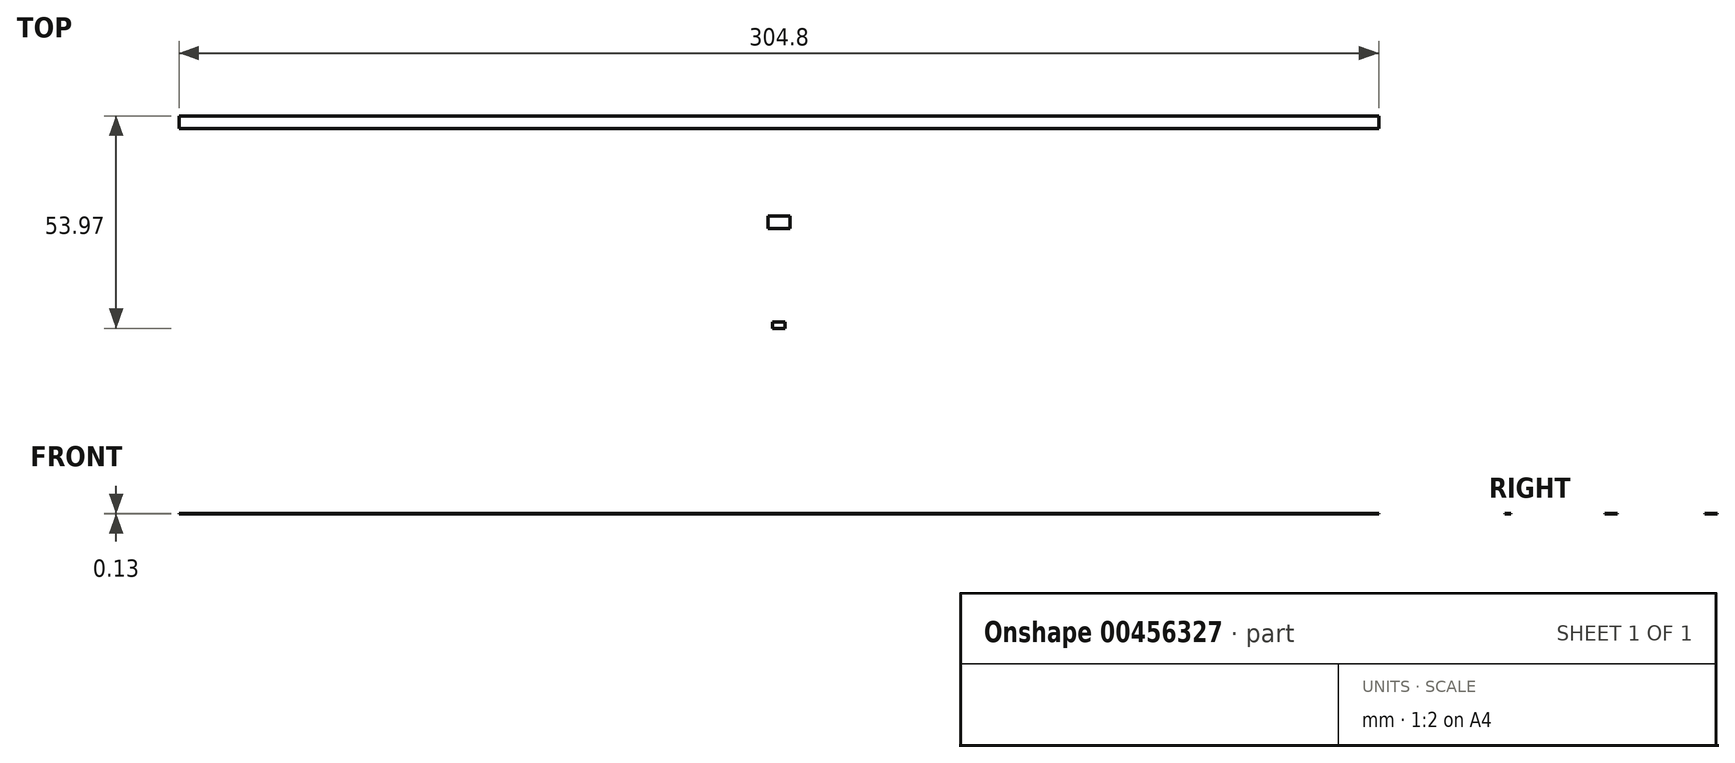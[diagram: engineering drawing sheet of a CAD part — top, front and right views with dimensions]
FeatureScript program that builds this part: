
annotation { "Feature Type Name" : "Feature", "Feature Type Description" : "" }
export const myFeature = defineFeature(function(context is Context, id is Id, definition is map)
    precondition{}
    {
        {
            var Q0;
            Q0=qCreatedBy(makeId("Top.planeOp"),FACE);
            var sketch = newSketch(context, id + "F0", { "sketchPlane" : qUnion([Q0])});
            skPoint(sketch, "E0", {"position": v(0, 0) * mm});
            skPoint(sketch, "E1", {"position": v(0, 3.18) * mm});
            skLineSegment(sketch, "E2", {"start": v(0, 0) * mm, "end": v(0, 0) * mm});
            skLineSegment(sketch, "E3", {"start": v(-152.4, 0) * mm, "end": v(152.4, 0) * mm});
            skPoint(sketch, "E4", {"position": v(-152.4, 3.18) * mm});
            skPoint(sketch, "E5", {"position": v(152.4, 3.18) * mm});
            skLineSegment(sketch, "E6", {"start": v(-152.4, 3.17) * mm, "end": v(152.4, 3.18) * mm});
            skLineSegment(sketch, "E7", {"start": v(152.4, 3.18) * mm, "end": v(152.4, 0) * mm});
            skLineSegment(sketch, "E8", {"start": v(-152.4, 3.18) * mm, "end": v(-152.4, 0) * mm});
            skSolve(sketch);
        }
        {
            var Q0;
            Q0=makeQuery(id+"F0.imprint","IMPRINT",FACE,{"disambiguationData":[TD([[makeQuery(id+"F0.imprint","IMPRINT",EDGE,{"derivedFrom":sQuery(id+"F0.wireOp",EDGE,"E3")}),1.0]])]});
            extrude(context, id + "F1", {"entities" : qUnion([Q0]), "depth" : 0.13 * mm});
        }
        {
            var Q0;
            Q0=qCreatedBy(makeId("Top.planeOp"),FACE);
            var sketch = newSketch(context, id + "F2", { "sketchPlane" : qUnion([Q0])});
            skPoint(sketch, "E9", {"position": v(0, -25.4) * mm});
            skPoint(sketch, "E10", {"position": v(-2.78, -25.4) * mm});
            skPoint(sketch, "E11", {"position": v(-2.78, -22.23) * mm});
            skPoint(sketch, "E12", {"position": v(0, -22.23) * mm});
            skLineSegment(sketch, "E13", {"start": v(0, -22.23) * mm, "end": v(-2.78, -22.23) * mm});
            skLineSegment(sketch, "E14", {"start": v(-2.78, -22.23) * mm, "end": v(-2.78, -25.4) * mm});
            skLineSegment(sketch, "E15", {"start": v(-2.78, -25.4) * mm, "end": v(0, -25.4) * mm});
            skLineSegment(sketch, "E16.MirrorCS", {"start": v(0, -22.23) * mm, "end": v(2.78, -22.23) * mm});
            skLineSegment(sketch, "E17.MirrorCS", {"start": v(2.78, -25.4) * mm, "end": v(0, -25.4) * mm});
            skLineSegment(sketch, "E18.MirrorCS", {"start": v(2.78, -22.23) * mm, "end": v(2.78, -25.4) * mm});
            skPoint(sketch, "E19.MirrorP", {"position": v(2.78, -25.4) * mm});
            skPoint(sketch, "E20.MirrorP", {"position": v(2.78, -22.23) * mm});
            skSolve(sketch);
        }
        {
            var Q0;
            Q0=makeQuery(id+"F2.imprint","IMPRINT",FACE,{"disambiguationData":[TD([[makeQuery(id+"F2.imprint","IMPRINT",EDGE,{"derivedFrom":sQuery(id+"F2.wireOp",EDGE,"E13")}),1.0]])]});
            extrude(context, id + "F3", {"entities" : qUnion([Q0]), "depth" : 0.13 * mm});
        }
        {
            var Q0;
            Q0=qCreatedBy(makeId("Top.planeOp"),FACE);
            var sketch = newSketch(context, id + "F4", { "sketchPlane" : qUnion([Q0])});
            skPoint(sketch, "E21", {"position": v(0, -50.8) * mm});
            skPoint(sketch, "E22", {"position": v(-1.59, -50.8) * mm});
            skPoint(sketch, "E23", {"position": v(-1.59, -49.21) * mm});
            skPoint(sketch, "E24", {"position": v(0, -49.21) * mm});
            skLineSegment(sketch, "E25", {"start": v(0, -49.21) * mm, "end": v(-1.59, -49.21) * mm});
            skLineSegment(sketch, "E26", {"start": v(-1.59, -49.21) * mm, "end": v(-1.59, -50.8) * mm});
            skLineSegment(sketch, "E27", {"start": v(-1.59, -50.8) * mm, "end": v(0, -50.8) * mm});
            skLineSegment(sketch, "E28.MirrorCS", {"start": v(0, -49.21) * mm, "end": v(1.59, -49.21) * mm});
            skLineSegment(sketch, "E29.MirrorCS", {"start": v(1.59, -49.21) * mm, "end": v(1.59, -50.8) * mm});
            skLineSegment(sketch, "E30.MirrorCS", {"start": v(1.59, -50.8) * mm, "end": v(0, -50.8) * mm});
            skPoint(sketch, "E31.MirrorP", {"position": v(1.59, -50.8) * mm});
            skPoint(sketch, "E32.MirrorP", {"position": v(1.59, -49.21) * mm});
            skSolve(sketch);
        }
        {
            var Q0;
            Q0=makeQuery(id+"F4.imprint","IMPRINT",FACE,{"disambiguationData":[TD([[makeQuery(id+"F4.imprint","IMPRINT",EDGE,{"derivedFrom":sQuery(id+"F4.wireOp",EDGE,"E25")}),1.0]])]});
            extrude(context, id + "F5", {"entities" : qUnion([Q0]), "depth" : 0.13 * mm});
        }
    });
